# Revit family: TYCO-FPP-FireClass-FC410SIO SINGLE IO MODULE
name_source: partatom
category: Electrical Fixtures
revit_build: Autodesk Revit 2014 (Build: 20130308_1515(x64)
units: mm (PartAtom-declared; Revit-internal decimal feet)

## types (1)
- TYCO-FPP-FireClass-FC410SIO SINGLE IO MODULE
    Alarm resistor = 680Ω
    Description = FC410SIO  SINGLE IO MODULE
    EOL = 3k3
    Front cover = Yes
    Keynote = The FC410SIO Single Input/Output Module is designed to provide
a monitored open collector input and a volt free relay changeover
output. FC410SIO can switch up to 2 A @ 24 Vdc.
    Length = 65 mm
    Manufacturer = Tyco
    Model = FireClass - 555.800.763
    Operating Humidity = Up to 95% non condensing
    Operating Temperature = -25o to +70oC
    PCB = PCB
    Rear cover = Yes
    Storage Temperature = -40o to +80oC
    Type Comments = Single Input/Ouput Unit
    URL = https://fireclass.co.uk
    Voltage = 2A @ 24V dc
    Width = 85 mm
    Wire Size = Min 1.5mm2

## geometry (parser evidence)
native form markers: Sweep x7
no freeform markers — native parametric forms only
